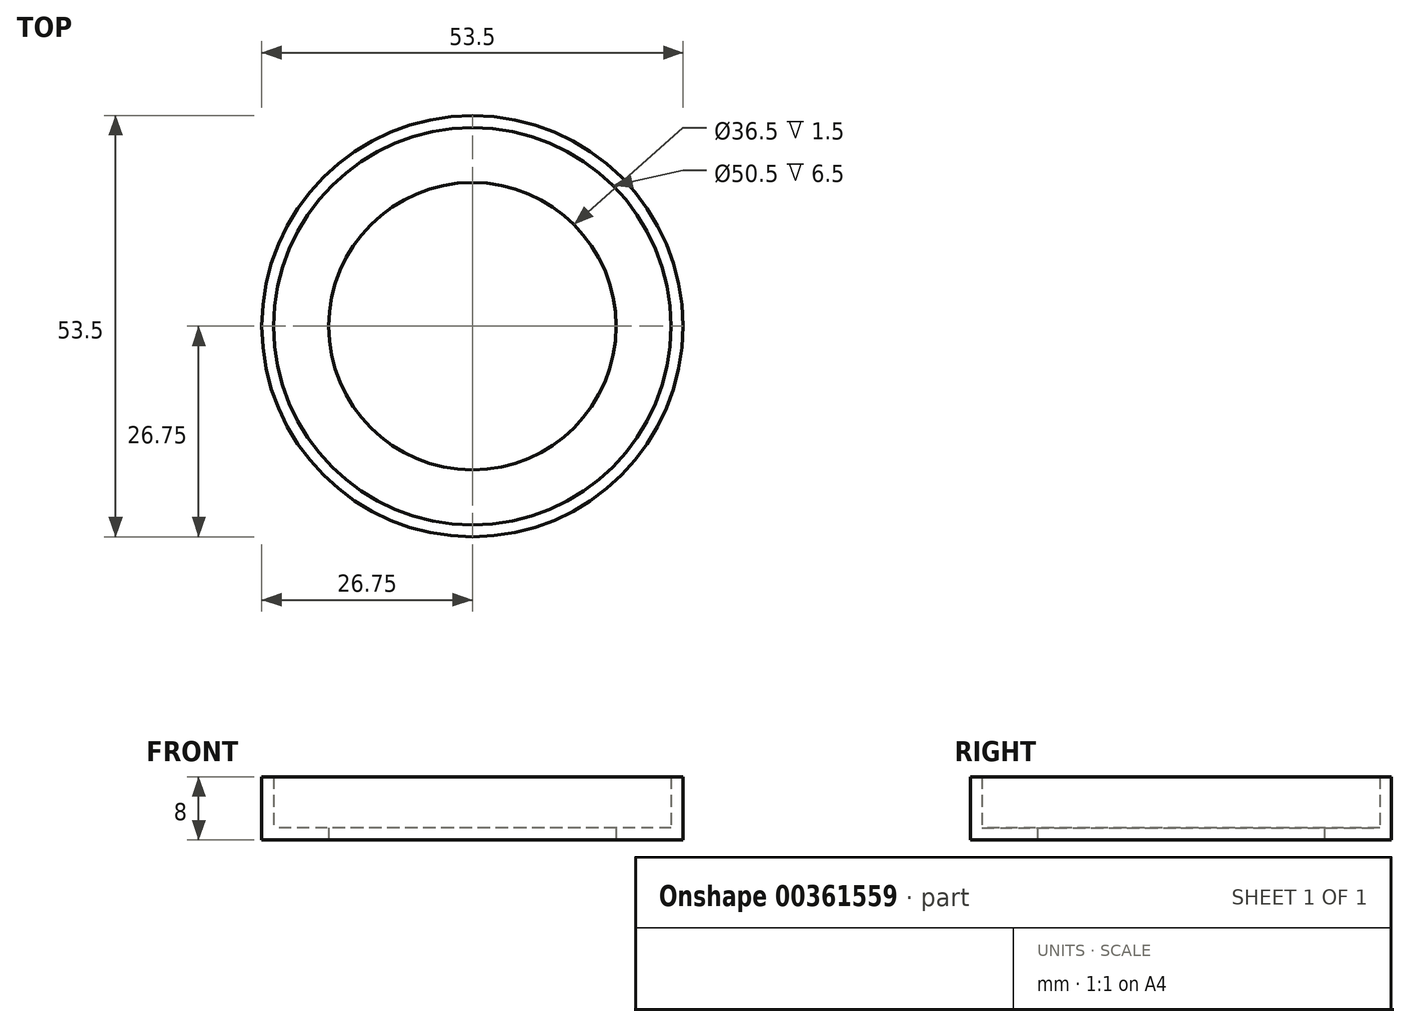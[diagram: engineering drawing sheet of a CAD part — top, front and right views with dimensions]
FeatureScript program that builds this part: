
annotation { "Feature Type Name" : "Feature", "Feature Type Description" : "" }
export const myFeature = defineFeature(function(context is Context, id is Id, definition is map)
    precondition{}
    {
        {
            var Q0;
            Q0=qCreatedBy(makeId("Top.planeOp"),FACE);
            var sketch = newSketch(context, id + "F0", { "sketchPlane" : qUnion([Q0])});
            skCircle(sketch, "E0", {"center": v(0, 0) * mm, "radius": 25.25 * mm});
            skCircle(sketch, "E1.0", {"center": v(0, 0) * mm, "radius": 18.25 * mm});
            skSolve(sketch);
        }
        {
            var Q0;
            Q0=makeQuery(id+"F0.imprint","IMPRINT",FACE,{"disambiguationData":[TD([[makeQuery(id+"F0.imprint","IMPRINT",EDGE,{"derivedFrom":sQuery(id+"F0.wireOp",EDGE,"E0")}),-1.0]])]});
            var Q1;
            Q1=makeQuery(id+"F0.imprint","IMPRINT",FACE,{"disambiguationData":[TD([[makeQuery(id+"F0.imprint","IMPRINT",EDGE,{"derivedFrom":sQuery(id+"F0.wireOp",EDGE,"E0")}),1.0]])]});
            extrude(context, id + "F1", {"entities" : qUnion([Q0, Q1]), "depth" : 1.5 * mm});
        }
        {
            var Q0;
            Q0=qCreatedBy(makeId("Top.planeOp"),FACE);
            var sketch = newSketch(context, id + "F2", { "sketchPlane" : qUnion([Q0])});
            skCircle(sketch, "E2", {"center": v(0, 0) * mm, "radius": 25.25 * mm});
            skCircle(sketch, "E3.0", {"center": v(0, 0) * mm, "radius": 26.75 * mm});
            skSolve(sketch);
        }
        {
            var Q0;
            Q0=makeQuery(id+"F2.imprint","IMPRINT",FACE,{"disambiguationData":[TD([[makeQuery(id+"F2.imprint","IMPRINT",EDGE,{"derivedFrom":sQuery(id+"F2.wireOp",EDGE,"E2")}),-1.0]])]});
            extrude(context, id + "F3", {"entities" : qUnion([Q0]), "operationType" : NewBodyOperationType.ADD, "depth" : 8 * mm});
        }
    });
